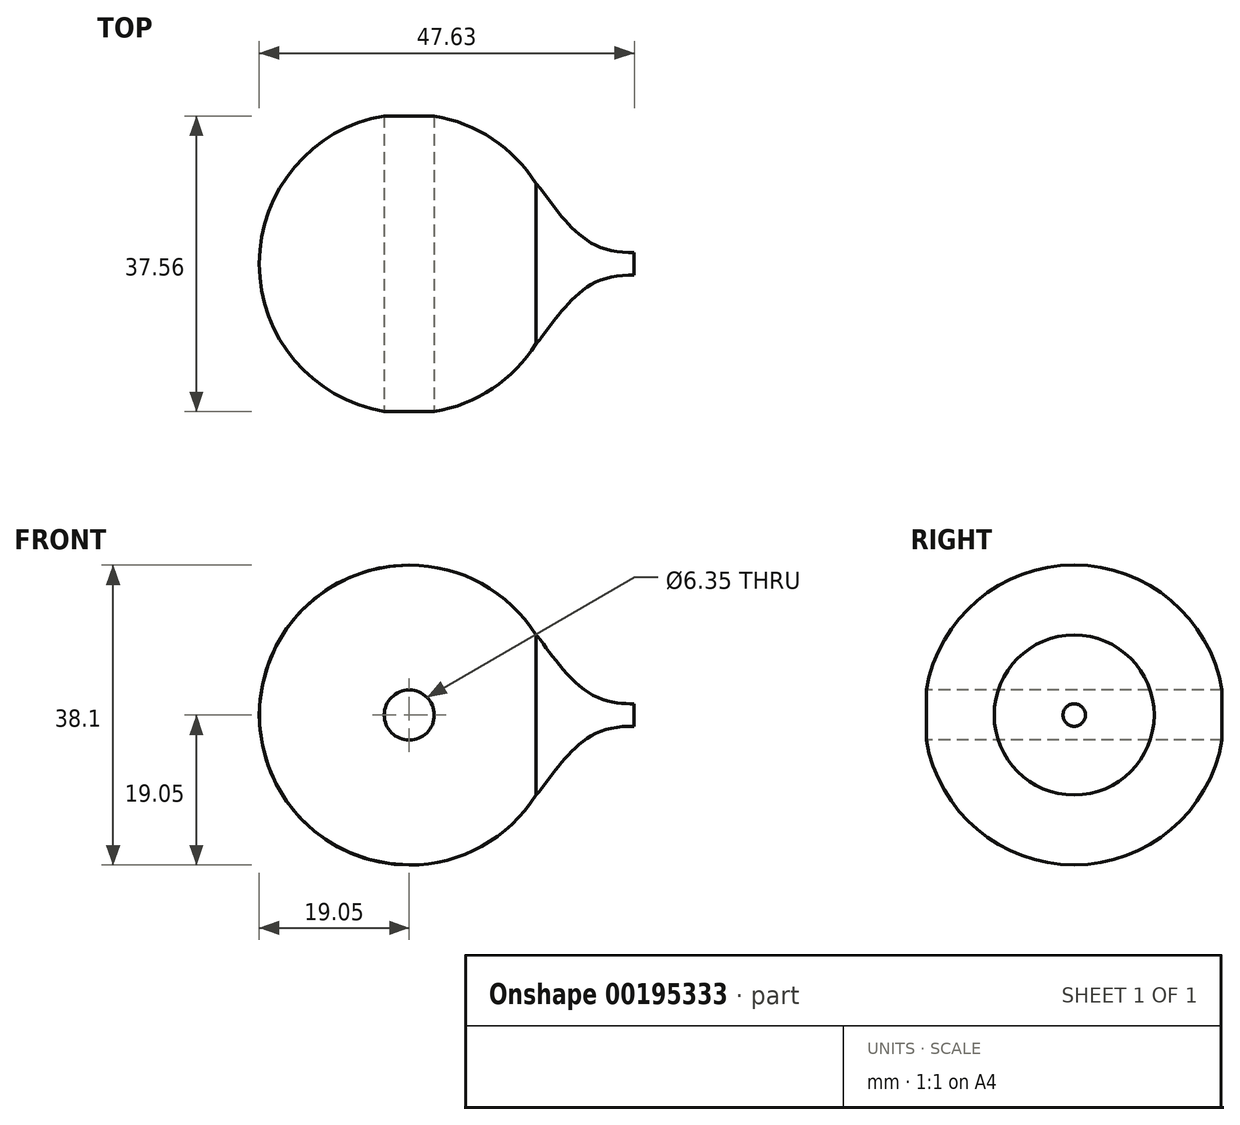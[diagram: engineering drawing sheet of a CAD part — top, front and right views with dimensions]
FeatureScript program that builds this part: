
annotation { "Feature Type Name" : "Feature", "Feature Type Description" : "" }
export const myFeature = defineFeature(function(context is Context, id is Id, definition is map)
    precondition{}
    {
        {
            var Q0;
            Q0=qCreatedBy(makeId("Front.planeOp"),FACE);
            var sketch = newSketch(context, id + "F0", { "sketchPlane" : qUnion([Q0])});
            skArc(sketch, "E0", {"start": v(0, -19.05) * mm, "mid": v(19.05, 0) * mm, "end": v(0, 19.05) * mm});
            skLineSegment(sketch, "E1", {"start": v(0, 19.05) * mm, "end": v(0, -19.05) * mm});
            skSolve(sketch);
        }
        {
            var Q0;
            Q0 = qSketchRegion(id + "F0", true);
            var Q1;
            Q1=sQuery(id+"F0.wireOp",EDGE,"E1");
            revolve(context, id + "F1", {"entities" : qUnion([Q0]), "axis" : qUnion([Q1]), "revolveType" : RevolveType.FULL});
        }
        {
            var Q0;
            Q0=qCreatedBy(makeId("Right.planeOp"),FACE);
            cPlane(context, id + "F2", {"entities" : qUnion([Q0]), "cplaneType" : CPlaneType.OFFSET, "offset" : 12.7 * mm, "width" : 152.4 * mm, "height" : 152.4 * mm});
        }
        {
            var Q0;
            Q0=qCreatedBy(id+"F2.planeOp",FACE);
            var sketch = newSketch(context, id + "F3", { "sketchPlane" : qUnion([Q0])});
            skCircle(sketch, "E2", {"center": v(0, 0) * mm, "radius": 10.16 * mm});
            skSolve(sketch);
        }
        {
            var Q0;
            Q0 = qSketchRegion(id + "F3", true);
            extrude(context, id + "F4", {"entities" : qUnion([Q0]), "operationType" : NewBodyOperationType.ADD, "depth" : 15.88 * mm});
        }
        {
            var Q0;
            Q0=qCreatedBy(makeId("Top.planeOp"),FACE);
            var sketch = newSketch(context, id + "F5", { "sketchPlane" : qUnion([Q0])});
            skFitSpline(sketch, "E3", {"points": [v(16.03, -10.36) * mm, v(23.4, -2.48) * mm, v(30.19, -1.5) * mm], "startDerivative": vector(8.24, 10.36) * mm, "endDerivative": vector(8.77, -0.36) * mm});
            skLineSegment(sketch, "E4", {"start": v(16.03, -10.36) * mm, "end": v(30.19, -10.36) * mm});
            skLineSegment(sketch, "E5", {"start": v(30.19, -10.36) * mm, "end": v(30.19, -1.5) * mm});
            skLineSegment(sketch, "E6", {"start": v(30.11, 0) * mm, "end": v(16.6, 0) * mm});
            skSolve(sketch);
        }
        {
            var Q0;
            Q0=makeQuery(id+"F5.imprint","IMPRINT",FACE,{"disambiguationData":[TD([[makeQuery(id+"F5.imprint","IMPRINT",EDGE,{"derivedFrom":sQuery(id+"F5.wireOp",EDGE,"E3")}),-1.0]])]});
            var Q1;
            Q1=sQuery(id+"F5.wireOp",EDGE,"E5");
            var Q2;
            Q2=sQuery(id+"F5.wireOp",EDGE,"E4");
            var Q3;
            Q3=sQuery(id+"F5.wireOp",EDGE,"E3");
            var Q4;
            Q4=sQuery(id+"F5.wireOp",EDGE,"E6");
            revolve(context, id + "F6", {"operationType" : NewBodyOperationType.REMOVE, "entities" : qUnion([Q0]), "surfaceEntities" : qUnion([Q1, Q2, Q3]), "axis" : qUnion([Q4]), "revolveType" : RevolveType.FULL, "oppositeDirection" : true});
        }
        {
            var Q0;
            Q0=qCreatedBy(makeId("Front.planeOp"),FACE);
            var sketch = newSketch(context, id + "F7", { "sketchPlane" : qUnion([Q0])});
            skCircle(sketch, "E7", {"center": v(0, 0) * mm, "radius": 3.18 * mm});
            skSolve(sketch);
        }
        {
            var Q0;
            Q0 = qSketchRegion(id + "F7", true);
            extrude(context, id + "F8", {"entities" : qUnion([Q0]), "operationType" : NewBodyOperationType.REMOVE, "endBound" : BoundingType.SYMMETRIC, "oppositeDirection" : true, "depth" : 50.8 * mm});
        }
        {
            var Q0;
            Q0=makeQuery(id+"F6.boolean.opBoolean","INTERSECT",EDGE,{"derivedFrom":[makeQuery(id+"F4.opExtrude","SWEPT_FACE",FACE,{"disambiguationData":[OSD([sQuery(id+"F3.wireOp",EDGE,"E2")])]}),makeQuery(id+"F6.opRevolve","SWEPT_FACE",FACE,{"disambiguationData":[OSD([sQuery(id+"F5.wireOp",EDGE,"E3")])]})]});
            fillet(context, id + "F9", {"entities" : qUnion([Q0]), "radius" : 5.08 * mm, "tangentPropagation" : true, "allowEdgeOverflow" : false});
        }
    });
